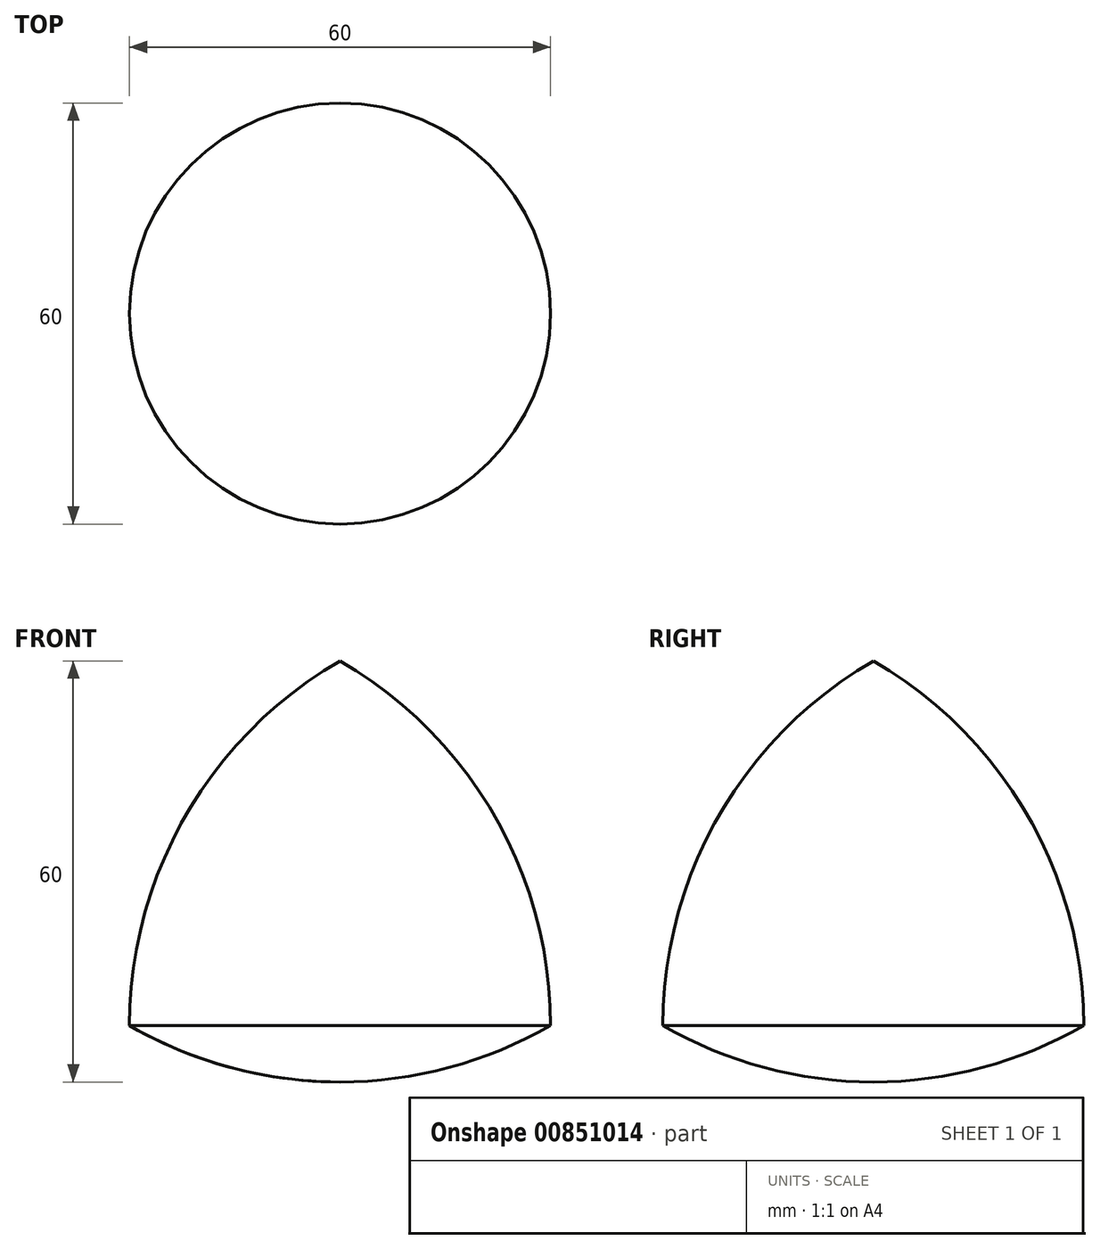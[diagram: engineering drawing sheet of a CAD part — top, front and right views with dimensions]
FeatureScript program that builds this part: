
annotation { "Feature Type Name" : "Feature", "Feature Type Description" : "" }
export const myFeature = defineFeature(function(context is Context, id is Id, definition is map)
    precondition{}
    {
        {
            var Q0;
            Q0=qCreatedBy(makeId("Front.planeOp"),FACE);
            var sketch = newSketch(context, id + "F0", { "sketchPlane" : qUnion([Q0])});
            skLineSegment(sketch, "E0", {"start": v(-30, -17.32) * mm, "end": v(0, 34.64) * mm, "construction": true});
            skLineSegment(sketch, "E1", {"start": v(0, 34.64) * mm, "end": v(30, -17.32) * mm, "construction": true});
            skLineSegment(sketch, "E2", {"start": v(30, -17.32) * mm, "end": v(-30, -17.32) * mm, "construction": true});
            skLineSegment(sketch, "E3", {"start": v(-15, 8.66) * mm, "end": v(30, -17.32) * mm, "construction": true});
            skLineSegment(sketch, "E4", {"start": v(15, 8.66) * mm, "end": v(-30, -17.32) * mm, "construction": true});
            skPoint(sketch, "E5", {"position": v(0, 0) * mm});
            skArc(sketch, "E6", {"start": v(0, 34.64) * mm, "mid": v(-21.96, 12.68) * mm, "end": v(-30, -17.32) * mm});
            skLineSegment(sketch, "E7", {"start": v(0, 34.64) * mm, "end": v(0, -25.36) * mm});
            skArc(sketch, "E8", {"start": v(-30, -17.32) * mm, "mid": v(-15.53, -23.31) * mm, "end": v(0, -25.36) * mm});
            skSolve(sketch);
        }
        {
            var Q0;
            Q0 = qSketchRegion(id + "F0", true);
            var Q1;
            Q1=sQuery(id+"F0.wireOp",EDGE,"E7");
            revolve(context, id + "F1", {"surfaceOperationType" : NewSurfaceOperationType.NEW, "entities" : qUnion([Q0]), "axis" : qUnion([Q1]), "revolveType" : RevolveType.FULL});
        }
    });
